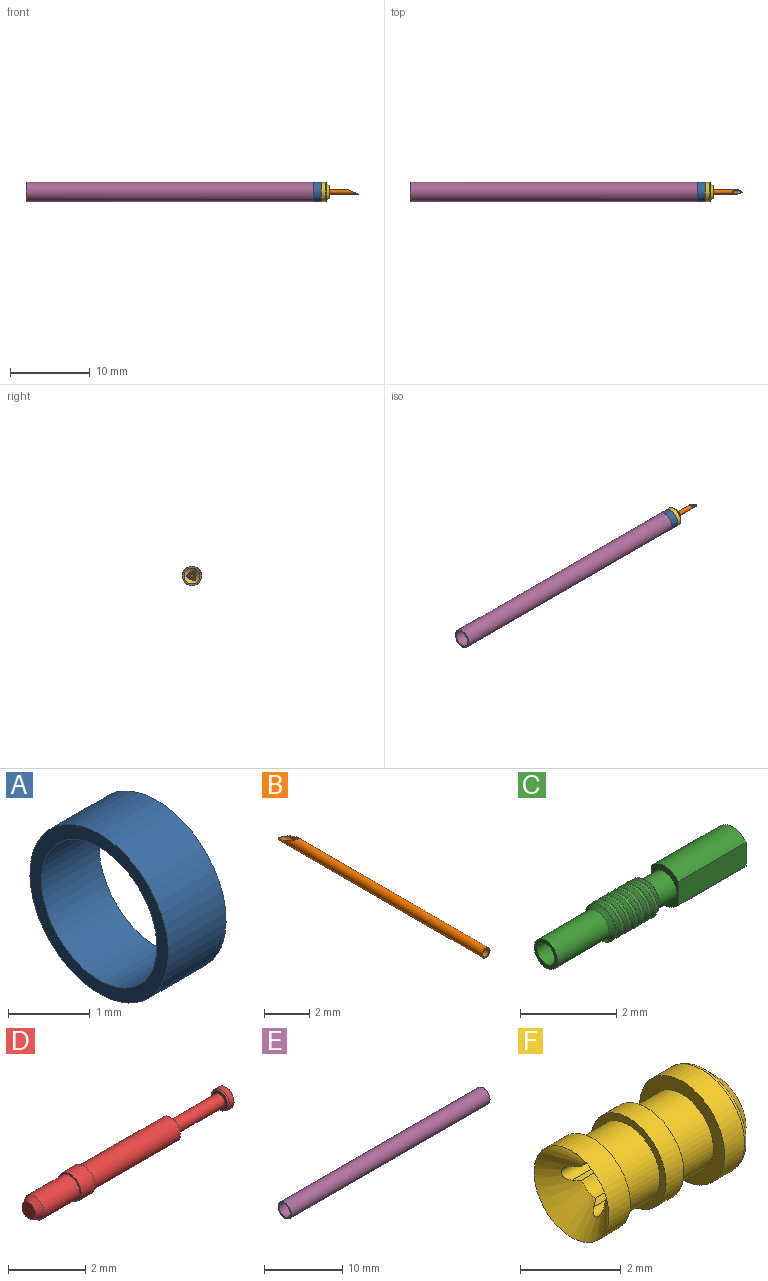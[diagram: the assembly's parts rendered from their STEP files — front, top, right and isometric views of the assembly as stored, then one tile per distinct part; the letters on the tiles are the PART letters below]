
ASSEMBLY  parts=6 mates=5
PART A: 4 faces, bbox 1x2.4x2.4 mm
  f0: cylinder r=1mm len=2mm, axis (-1,0,0), area 6.3mm2, adj f2,f3
  f1: cylinder r=1.2mm len=2.4mm, axis (-1,0,0), area 7.5mm2, adj f2,f3
  f2: plane 2.4x2.4mm, normal (1,0,0), area 1.4mm2, adj f0,f1
  f3: plane 2.4x2.4mm, normal (-1,0,0), area 1.4mm2, adj f0,f1
PART B: 6 faces, bbox 0.5x13x0.5 mm
  f0: cylinder r=0.2mm len=12.88mm, axis (0,1,0), area 16mm2, adj f2,f3
  f1: cylinder r=0.26mm len=13mm, axis (0,1,0), area 19.8mm2, adj f2,f3,f4,f5
  f2: plane 1.21x0.52mm, normal (0,0.39,0.92), area 0.1mm2, adj f0,f1,f4,f5
  f3: plane 0.51x0.51mm, normal (0,-1,0), area 0.1mm2, adj f0,f1
  f4: plane 0.36x0.23mm, normal (-0.84,0.54,0), area 0mm2, adj f1,f2
  f5: plane 0.36x0.23mm, normal (0.84,0.54,0), area 0mm2, adj f1,f2
PART C: 15 faces, bbox 5.5x0.9x1.1 mm
  f0: cone r=0.45mm half-angle=45deg, axis (1,0,0), area 0.3mm2, adj f4,f5,f13,f14
  f1: cone r=0.35mm half-angle=45deg, axis (-1,0,0), area 0.3mm2, adj f2,f5,f13,f14
  f2: cylinder r=0.35mm len=0.7mm, axis (1,0,0), area 1.1mm2, adj f1,f9
  f3: cylinder r=0.26mm len=5.5mm, axis (1,0,0), area 8.8mm2, adj f6,f10
  f4: cylinder r=0.35mm len=1.5mm, axis (1,0,0), area 3.3mm2, adj f0,f10
  f5: cylinder r=0.45mm len=1.3mm, axis (1,0,0), area 1.3mm2, adj f0,f1,f13,f14
  f6: plane 1x0.8mm, normal (1,0,0), area 0.5mm2, adj f3,f7,f8,f11,f12
  f7: cylinder r=0.5mm len=2mm, axis (1,0,0), area 1.9mm2, adj f6,f9,f11,f12
  f8: cylinder r=0.5mm len=2mm, axis (1,0,0), area 1.9mm2, adj f6,f9,f11,f12
  f9: plane 1x0.8mm, normal (-1,0,0), area 0.3mm2, adj f2,f7,f8,f11,f12
  f10: plane 0.7x0.7mm, normal (-1,0,0), area 0.2mm2, adj f3,f4
  f11: plane 2x0.6mm, normal (0,1,0), area 1.2mm2, adj f6,f7,f8,f9
  f12: plane 2x0.6mm, normal (0,-1,0), area 1.2mm2, adj f6,f7,f8,f9
  f13: bspline ~1.51x1.05mm, area 1.5mm2, adj f0,f1,f5,f14
  f14: bspline ~1.51x1.05mm, area 1.5mm2, adj f0,f1,f5,f13
PART D: 13 faces, bbox 7.3x0.8x0.8 mm
  f0: plane 0.5x0.5mm, normal (-1,0,0), area 0.2mm2, adj f12
  f1: sphere r=0.43mm, area 0.4mm2, adj f2
  f2: cylinder r=0.32mm len=0.64mm, axis (-1,0,0), area 0.3mm2, adj f1,f3
  f3: cone r=0.3mm half-angle=21.8deg, axis (1,0,0), area 0.1mm2, adj f2,f4
  f4: plane 0.6x0.6mm, normal (-1,0,0), area 0.2mm2, adj f3,f5
  f5: cylinder r=0.2mm len=1.79mm, axis (-1,0,0), area 2.2mm2, adj f4,f6
  f6: plane 0.72x0.72mm, normal (1,0,0), area 0.3mm2, adj f5,f7
  f7: cylinder r=0.36mm len=3.2mm, axis (-1,0,0), area 7.2mm2, adj f6,f8
  f8: plane 0.84x0.84mm, normal (1,0,0), area 0.1mm2, adj f7,f9
  f9: cylinder r=0.42mm len=0.84mm, axis (-1,0,0), area 1.3mm2, adj f8,f10
  f10: plane 0.84x0.84mm, normal (-1,0,0), area 0.1mm2, adj f9,f11
  f11: cylinder r=0.36mm len=1.3mm, axis (-1,0,0), area 2.9mm2, adj f10,f12
  f12: cone r=0.25mm half-angle=28.8deg, axis (1,0,0), area 0.4mm2, adj f0,f11
PART E: 4 faces, bbox 35.9x2.4x2.4 mm
  f0: cylinder r=1mm len=35.9mm, axis (-1,0,0), area 225.6mm2, adj f1,f3
  f1: plane 2.4x2.4mm, normal (1,0,0), area 1.4mm2, adj f0,f2
  f2: cylinder r=1.2mm len=35.9mm, axis (-1,0,0), area 270.7mm2, adj f1,f3
  f3: plane 2.4x2.4mm, normal (-1,0,0), area 1.4mm2, adj f0,f2
PART F: 29 faces, bbox 4.1x2.6x2.6 mm
  f0: cylinder r=0.4mm len=3.35mm, axis (-1,0,0), area 1.6mm2, adj f2,f5,f19,f24
  f1: cylinder r=0.4mm len=3.35mm, axis (-1,0,0), area 1.6mm2, adj f3,f5,f23,f26
  f2: cone r=0.5mm half-angle=45deg, axis (1,0,0), area 0.1mm2, adj f0,f4,f19,f24
  f3: cone r=0.5mm half-angle=45deg, axis (1,0,0), area 0.1mm2, adj f1,f4,f23,f26
  f4: plane 1.5x1.5mm, normal (1,0,0), area 0.8mm2, adj f2,f3,f6,f18,f19,f20,f21,f22
  f5: cone r=1.05mm half-angle=45deg, axis (-1,0,0), area 3.8mm2, adj f0,f1,f16,f17,f18,f19,f20,f21
  f6: cone r=0.5mm half-angle=45deg, axis (1,0,0), area 0.1mm2, adj f4,f17,f18,f21
  f7: cone r=0.79mm half-angle=45deg, axis (-1,0,0), area 3mm2, adj f27,f28
  f8: cylinder r=1.19mm len=2.38mm, axis (-1,0,0), area 4.2mm2, adj f9,f28
  f9: plane 2.38x2.38mm, normal (-1,0,0), area 2mm2, adj f8,f10
  f10: cylinder r=0.88mm len=1.75mm, axis (-1,0,0), area 5.5mm2, adj f9,f11
  f11: plane 2.1x2.1mm, normal (1,0,0), area 1.1mm2, adj f10,f12
  f12: cylinder r=1.05mm len=2.1mm, axis (-1,0,0), area 3.3mm2, adj f11,f13
  f13: plane 2.1x2.1mm, normal (-1,0,0), area 1.1mm2, adj f12,f14
  f14: cylinder r=0.88mm len=1.75mm, axis (-1,0,0), area 5.5mm2, adj f13,f15
  f15: plane 2.1x2.1mm, normal (1,0,0), area 1.1mm2, adj f14,f16
  f16: cylinder r=1.05mm len=2.1mm, axis (-1,0,0), area 4mm2, adj f5,f15
  f17: cylinder r=0.4mm len=3.35mm, axis (-1,0,0), area 1.6mm2, adj f5,f6,f18,f21
  f18: plane 3.58x0.14mm, normal (0,0,1), area 0.5mm2, adj f4,f5,f6,f17,f20
  f19: plane 3.59x0.15mm, normal (0,-0.02,-1), area 0.5mm2, adj f0,f2,f4,f5,f20
  f20: cylinder r=0.17mm len=3.58mm, axis (1,0,0), area 1.9mm2, adj f4,f5,f18,f19
  f21: plane 3.59x0.13mm, normal (0,-0.85,0.52), area 0.5mm2, adj f4,f5,f6,f17,f22
  f22: cylinder r=0.17mm len=3.58mm, axis (1,0,0), area 1.9mm2, adj f4,f5,f21,f23
  f23: plane 3.58x0.12mm, normal (0,0.87,-0.5), area 0.4mm2, adj f1,f3,f4,f5,f22
  f24: plane 3.58x0.12mm, normal (0,-0.87,-0.5), area 0.4mm2, adj f0,f2,f4,f5,f25
  f25: cylinder r=0.17mm len=3.58mm, axis (1,0,0), area 1.9mm2, adj f4,f5,f24,f26
  f26: plane 3.59x0.13mm, normal (0,0.88,0.48), area 0.5mm2, adj f1,f3,f4,f5,f25
  f27: torus R=0.75mm, axis (-1,0,0), area 0.4mm2, adj f4,f7
  f28: torus R=1.09mm, axis (1,0,0), area 0.6mm2, adj f7,f8
PLACE A t=(-40.86,-2.49,-0.36)mm
PLACE B rot(axis=(0,0,-1),90deg) t=(44.98,-2.49,-0.36)mm
PLACE C rot(axis=(1,0,0),90deg) t=(0.1,-2.49,-0.36)mm
PLACE D t=(27.08,-2.49,-0.36)mm
PLACE E t=(-40.86,-2.49,-0.36)mm
PLACE F t=(38.74,-2.49,-0.36)mm
MATE fastened E.f0 <-> F.f0  axis (1,0,0) through (39.38,-2.49,-0.36)mm
MATE fastened A.f0 <-> F.f0  axis (-1,0,0) through (40.38,-2.49,-0.36)mm
MATE slider B.f0 <-> F.f0  axis (1,0,0) through (38.52,-2.49,-0.36)mm
MATE fastened B.f0 <-> C.f0  axis (1,0,0) through (31.98,-2.49,-0.36)mm
MATE slider D.f2 <-> F.f0  axis (1,0,0) through (30.03,-2.49,-0.36)mm
